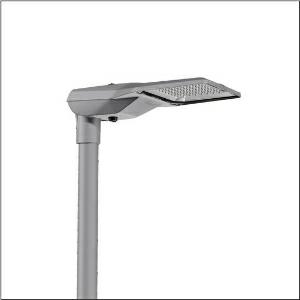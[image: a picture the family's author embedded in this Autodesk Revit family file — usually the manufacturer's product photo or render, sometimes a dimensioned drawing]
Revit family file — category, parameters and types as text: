
# Revit family: streetlight_sl_21_midi___pc-l_5xe3f43t08mb_dba8
name_source: partatom
category: Lighting Fixtures
units: mm (PartAtom-declared; Revit-internal decimal feet)

## family parameters
Cut with Voids When Loaded = No
Host = Face
Light Source = No
Part Type = Normal
Room Calculation Point = No
Round Connector Dimension = Use Diameter
Shared = No

## types (1)
- --- (1 x LED, 19200 lm, 147 W, 4000K)
    Apparent Load = 147 VA
    CIE Flux Codes = 38 78 98 100 100
    Color Rendering = 70
    Color Temperature = 4000K
    Default Elevation = 1800 mm
    Description = Streetlight SL 21 midi, mast luminaire, primary light control with lens, of PMMA, primary optical cover: cover, of toughened safety glass, transparent, light distribution: PC-L, light emission: direct distribution, primary light characteristic: asymmetric, left, installation type: side-entry, post-top, LED, High Power LED, rated luminous flux: 19.200lm, luminous efficacy: 131lm/W, light colour: 740, colour temperature: 4000K, control gear: D4i, control: overheat protection, constant luminous flux control, time-dependent luminous flux control, flexible luminous flux parameterisation, pre-setting: logarithmic dimming characteristic, mains connection: 230..240V, AC, 50/60Hz, start of lifetime: 147W, end of service life: 155W, reduction: 65W, luminaire housing, of diecast aluminium, powder-coated, Siteco® metallic grey (DB 702S), corrosivity category C5 mid according to DIN EN ISO 12944, please order mast flange separately, inclination adjustable: 0°, 5°, 10°, 15°, sealing non-destructively replaceable, multi-level sealing system, length: 644mm, width: 335mm, height: 110mm, mast flange for spigot size: 42mm (side-entry): 5XC10008XM4, 60/48mm (side-entry/post-top): 5XC10108XM2, 76/60mm (side-entry/post-top): 5XC10108XM1, mounting height: 4..8m, Smart Interface below and above, protection rating (complete): IP66, insulation class (complete): insulation class II (safety insulation), certification: CE, ENEC, ENEC+, VDE, impact resistance: IK10, permissible operating ambient temperature for outdoor applications: -40..+50°C, standard-compliant lighting for roads and squares, packaging unit: 1 piece

Light Distribution: PC-L
    Height = 111 mm
    Lamp = 1 x LED
    Lamp Light Flux = 19200 lm
    Lamp Power = 147 W
    Lamp count = 1
    Length = 644 mm
    Luminous efficacy = 131 lm/W
    Manufacturer = Siteco
    ModVariant = No
    Model = 5XE3F43T08MB
    Number of Poles = 1
    OnlyDefault = Yes
    Power Factor = 1
    Product Name = Streetlight SL 21 midi | PC-L
    Product group = mast luminaire | pylon top
    ProductGroupID = 6100
    Protection Class = Protection class II
    Protection Degree = IP 66
    RLX_Detail_Level = 1
    RLX_Emergency_Light_Flux = 0 lm
    RLX_Emergency_Type = 0
    RLX_Emergency_Type_DB = No
    RlxData = <blob elided: 29637 chars, md5=551d5d1a>
    Socket = socket
    Standby Power = 0 W
    System Light Flux = 19200 lm
    System Power = 147 W
    Type Comments = factory setting: luminous flux: 100 % | dim-lin: 254 | 750 mA
    Type Image = l_1004304.jpg
    URL = http://relux.com
    VarID = @adj_085687
    Voltage = 0 V
    Weight = 0.00 kg
    Width = 336 mm

## geometry (parser evidence)
native form markers: Blend x4, Sweep x10
no freeform markers — native parametric forms only
